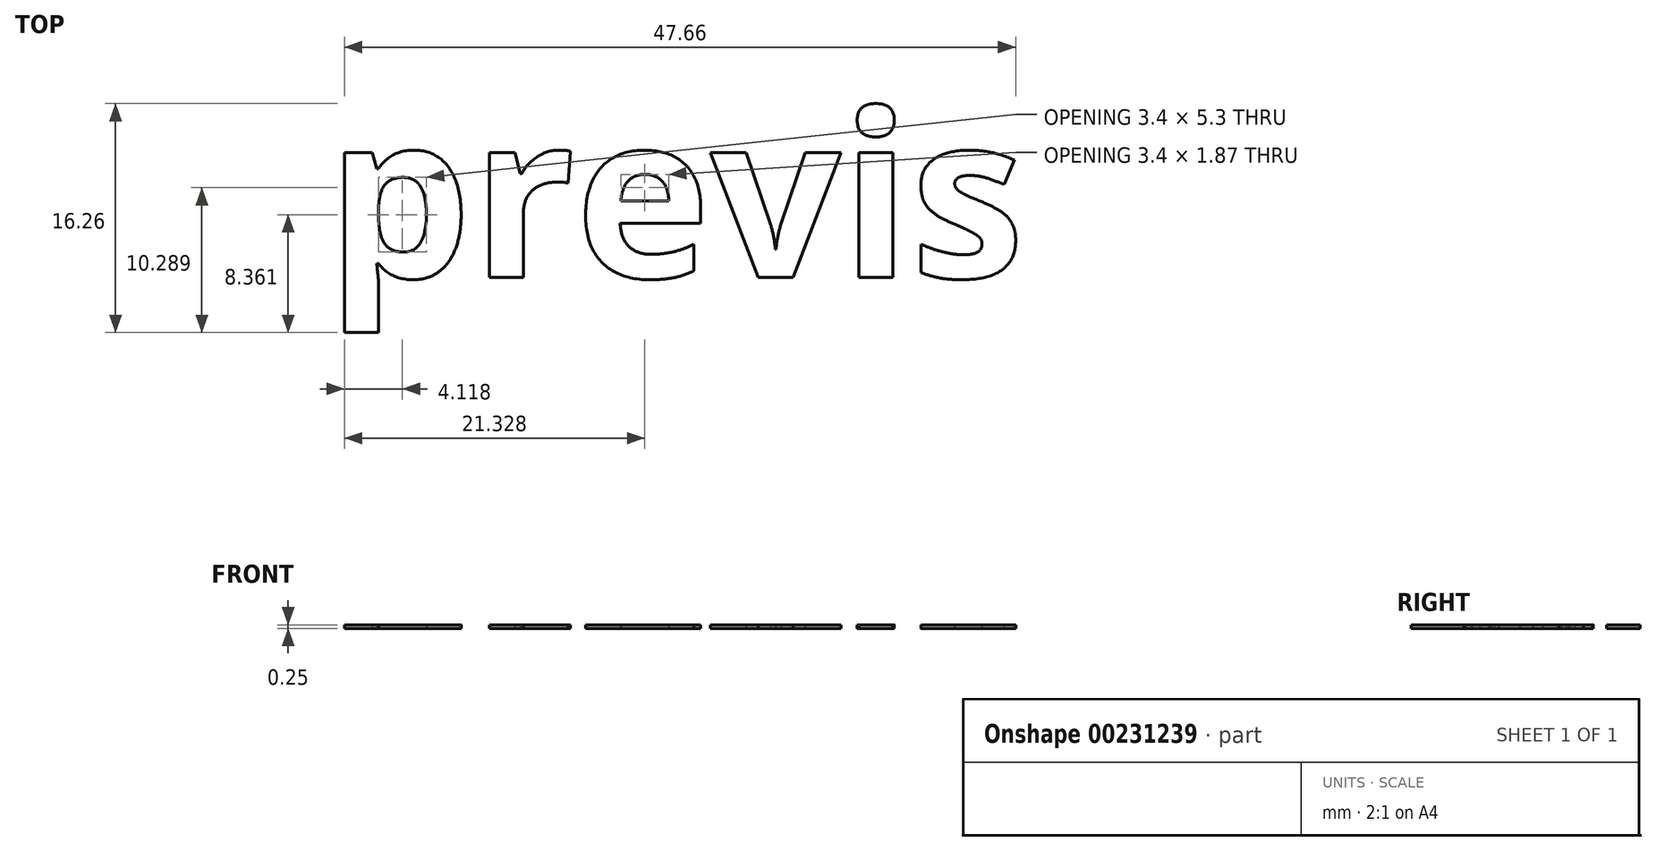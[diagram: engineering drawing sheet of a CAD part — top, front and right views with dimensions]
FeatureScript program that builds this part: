
annotation { "Feature Type Name" : "Feature", "Feature Type Description" : "" }
export const myFeature = defineFeature(function(context is Context, id is Id, definition is map)
    precondition{}
    {
        {
            var Q0;
            Q0=qCreatedBy(makeId("Top.planeOp"),FACE);
            var sketch = newSketch(context, id + "F0", { "sketchPlane" : qUnion([Q0])});
            skText(sketch, "E0", { "text": "previs", "fontName": "OpenSans-Bold.ttf"});
            const initialGuessF0  = {"E0": [-0.025, -0.005, 1, 0, 0.0117]};
            skSetInitialGuess(sketch, initialGuessF0);
            skSolve(sketch);
        }
        {
            var Q0;
            Q0 = qSketchRegion(id + "F0", true);
            extrude(context, id + "F1", {"entities" : qUnion([Q0]), "depth" : 0.25 * mm});
        }
    });
